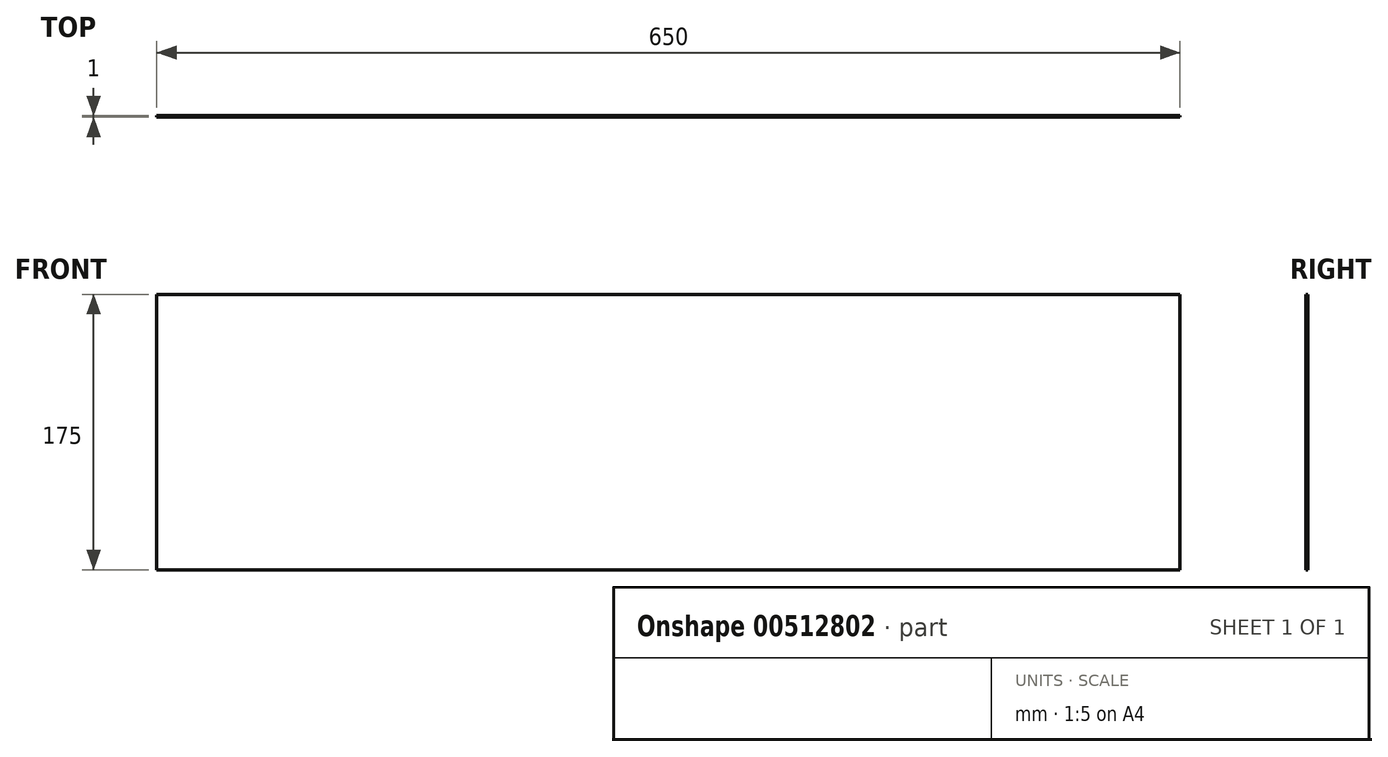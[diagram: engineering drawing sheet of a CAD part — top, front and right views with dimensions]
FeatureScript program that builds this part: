
annotation { "Feature Type Name" : "Feature", "Feature Type Description" : "" }
export const myFeature = defineFeature(function(context is Context, id is Id, definition is map)
    precondition{}
    {
        {
            var Q0;
            Q0=qCreatedBy(makeId("Front.planeOp"),FACE);
            var sketch = newSketch(context, id + "F0", { "sketchPlane" : qUnion([Q0])});
            skLineSegment(sketch, "E0.bottom", {"start": v(0, 0) * mm, "end": v(650, 0) * mm});
            skLineSegment(sketch, "E0.top", {"start": v(0, 175) * mm, "end": v(650, 175) * mm});
            skLineSegment(sketch, "E0.left", {"start": v(0, 0) * mm, "end": v(0, 175) * mm});
            skLineSegment(sketch, "E0.right", {"start": v(650, 0) * mm, "end": v(650, 175) * mm});
            skSolve(sketch);
        }
        {
            var Q0;
            Q0 = qSketchRegion(id + "F0", true);
            extrude(context, id + "F1", {"entities" : qUnion([Q0]), "depth" : 1 * mm, "offsetDistance" : 25 * mm});
        }
    });
